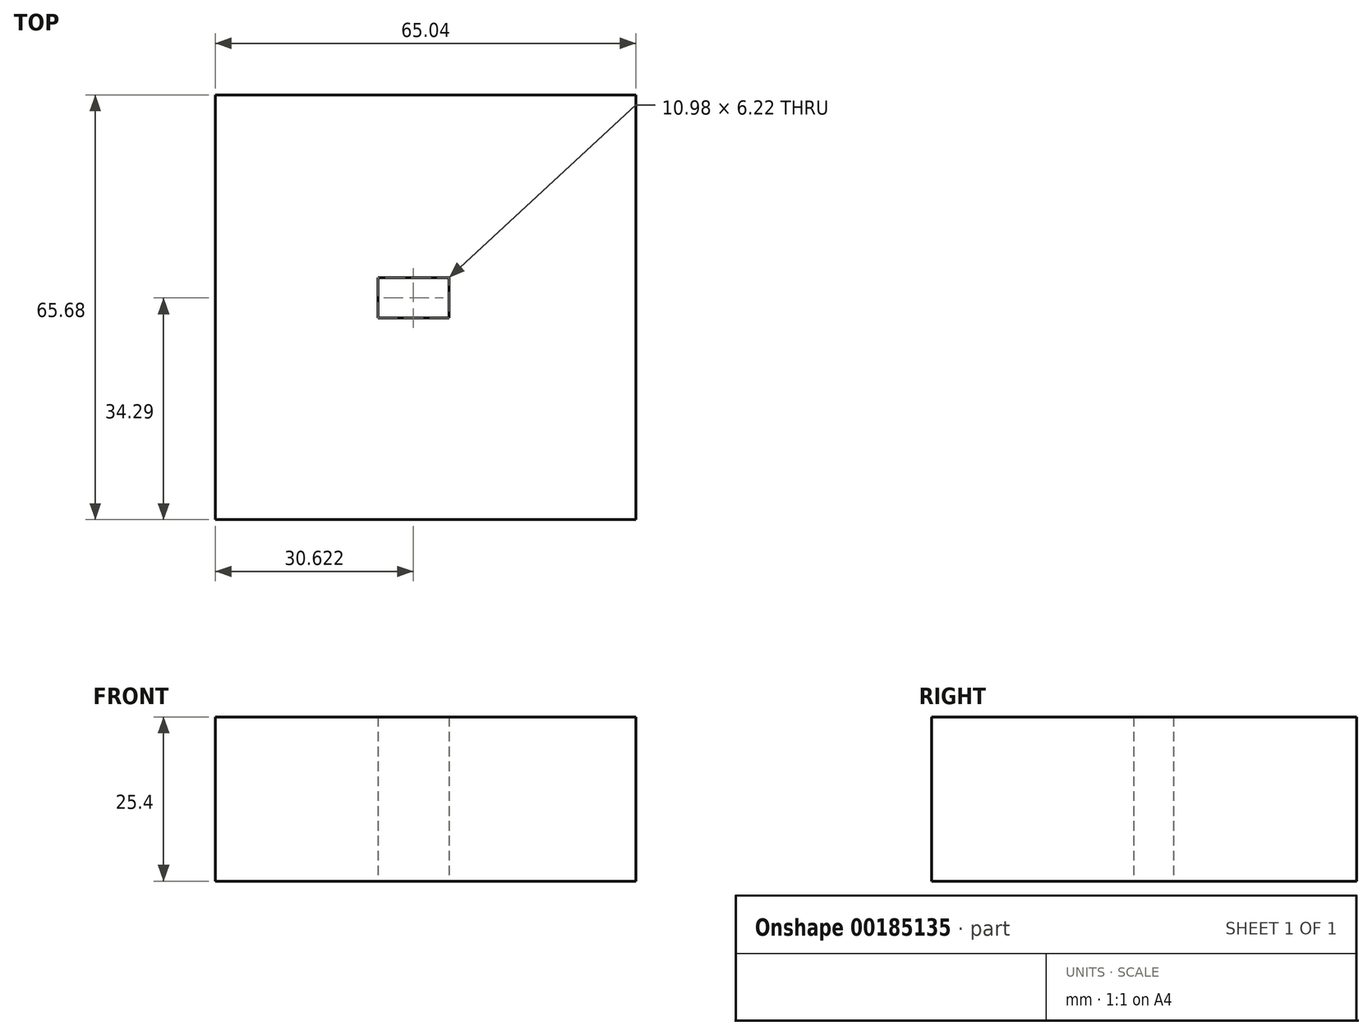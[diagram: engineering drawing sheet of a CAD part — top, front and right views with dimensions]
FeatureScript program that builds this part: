
annotation { "Feature Type Name" : "Feature", "Feature Type Description" : "" }
export const myFeature = defineFeature(function(context is Context, id is Id, definition is map)
    precondition{}
    {
        {
            var Q0;
            Q0=qCreatedBy(makeId("Top.planeOp"),FACE);
            var sketch = newSketch(context, id + "F0", { "sketchPlane" : qUnion([Q0])});
            skLineSegment(sketch, "E0.bottom", {"start": v(13.78, -37.4) * mm, "end": v(-51.26, -37.4) * mm});
            skLineSegment(sketch, "E0.top", {"start": v(13.78, 28.28) * mm, "end": v(-51.26, 28.28) * mm});
            skLineSegment(sketch, "E0.left", {"start": v(13.78, -37.4) * mm, "end": v(13.78, 28.28) * mm});
            skLineSegment(sketch, "E0.right", {"start": v(-51.26, -37.4) * mm, "end": v(-51.26, 28.28) * mm});
            skLineSegment(sketch, "E1.bottom", {"start": v(-26.13, -6.22) * mm, "end": v(-15.15, -6.22) * mm});
            skLineSegment(sketch, "E1.top", {"start": v(-26.13, 0) * mm, "end": v(-15.15, 0) * mm});
            skLineSegment(sketch, "E1.left", {"start": v(-26.13, -6.22) * mm, "end": v(-26.13, 0) * mm});
            skLineSegment(sketch, "E1.right", {"start": v(-15.15, -6.22) * mm, "end": v(-15.15, 0) * mm});
            skSolve(sketch);
        }
        {
            var Q0;
            Q0=makeQuery(id+"F0.imprint","IMPRINT",FACE,{"disambiguationData":[TD([[makeQuery(id+"F0.imprint","IMPRINT",EDGE,{"derivedFrom":sQuery(id+"F0.wireOp",EDGE,"E0.bottom")}),-1.0]])]});
            extrude(context, id + "F1", {"entities" : qUnion([Q0]), "depth" : 25.4 * mm});
        }
    });
